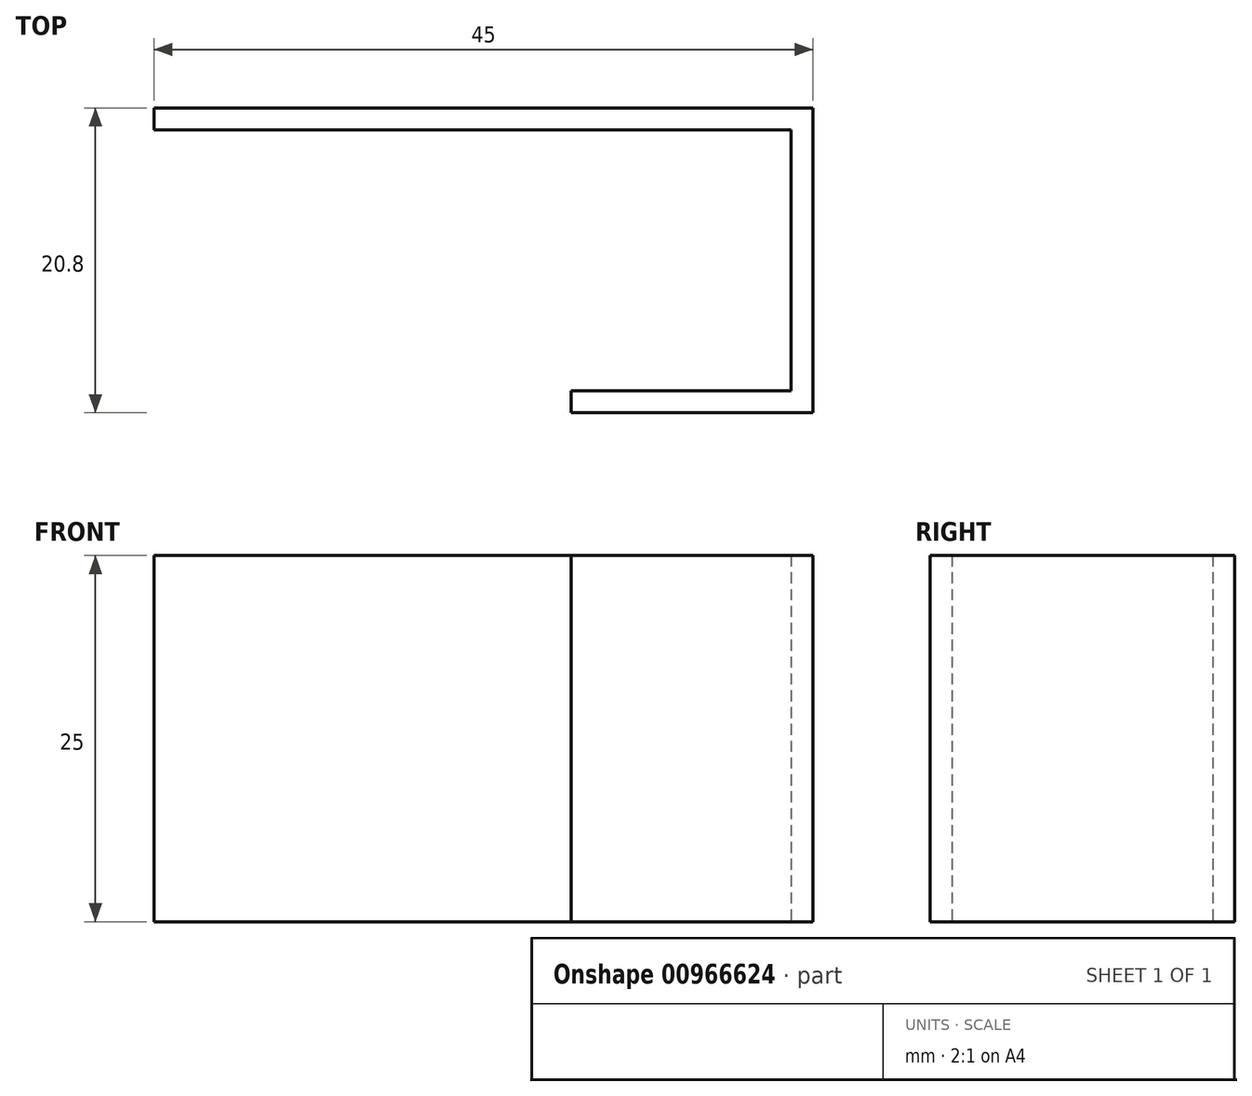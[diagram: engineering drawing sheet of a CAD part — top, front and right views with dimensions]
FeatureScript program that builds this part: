
annotation { "Feature Type Name" : "Feature", "Feature Type Description" : "" }
export const myFeature = defineFeature(function(context is Context, id is Id, definition is map)
    precondition{}
    {
        {
            var Q0;
            Q0=qCreatedBy(makeId("Top.planeOp"),FACE);
            var sketch = newSketch(context, id + "F0", { "sketchPlane" : qUnion([Q0])});
            skLineSegment(sketch, "E0", {"start": v(-7.78, 4.75) * mm, "end": v(37.22, 4.75) * mm});
            skLineSegment(sketch, "E1", {"start": v(37.22, 4.75) * mm, "end": v(37.22, -16.05) * mm});
            skLineSegment(sketch, "E2", {"start": v(37.22, -16.05) * mm, "end": v(20.72, -16.05) * mm});
            skLineSegment(sketch, "E3", {"start": v(20.72, -16.05) * mm, "end": v(20.72, -14.55) * mm});
            skLineSegment(sketch, "E4", {"start": v(20.72, -14.55) * mm, "end": v(35.72, -14.55) * mm});
            skLineSegment(sketch, "E5", {"start": v(35.72, -14.55) * mm, "end": v(35.72, 3.25) * mm});
            skLineSegment(sketch, "E6", {"start": v(35.72, 3.25) * mm, "end": v(-7.78, 3.25) * mm});
            skLineSegment(sketch, "E7", {"start": v(-7.78, 3.25) * mm, "end": v(-7.78, 4.75) * mm});
            skLineSegment(sketch, "E8", {"start": v(35.72, 3.25) * mm, "end": v(37.22, 3.25) * mm, "construction": true});
            skSolve(sketch);
        }
        {
            var Q0;
            Q0=makeQuery(id+"F0.imprint","IMPRINT",FACE,{"disambiguationData":[TD([[makeQuery(id+"F0.imprint","IMPRINT",EDGE,{"derivedFrom":sQuery(id+"F0.wireOp",EDGE,"E0")}),-1.0]])]});
            extrude(context, id + "F1", {"entities" : qUnion([Q0]), "depth" : 25 * mm, "offsetDistance" : 25 * mm});
        }
    });
